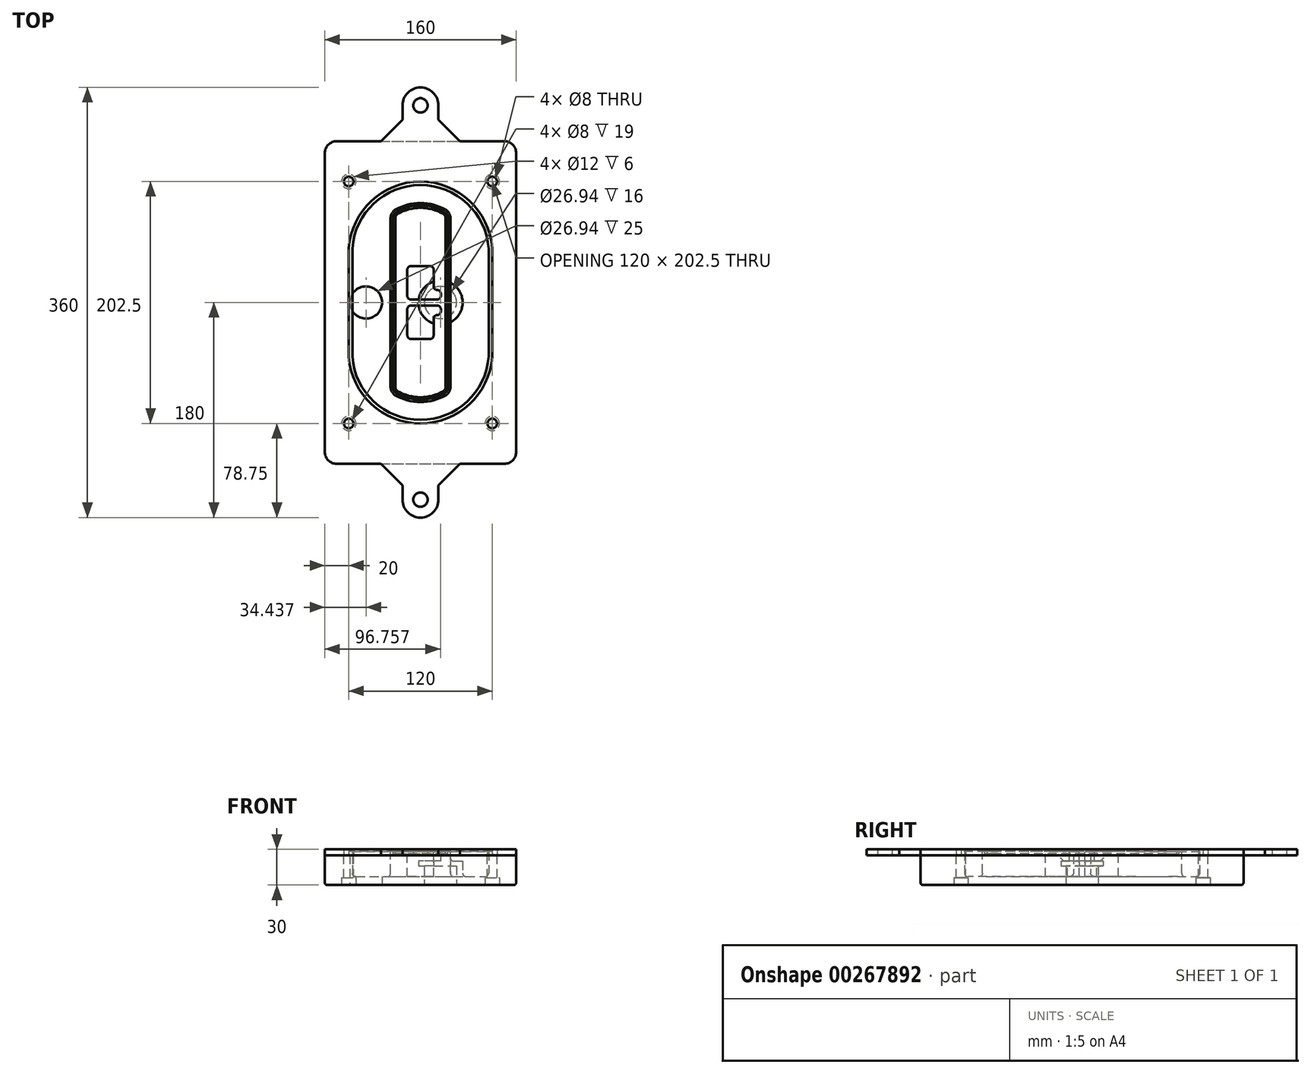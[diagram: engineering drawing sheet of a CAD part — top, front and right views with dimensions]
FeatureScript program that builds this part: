
annotation { "Feature Type Name" : "Feature", "Feature Type Description" : "" }
export const myFeature = defineFeature(function(context is Context, id is Id, definition is map)
    precondition{}
    {
        {
            var Q0;
            Q0=qCreatedBy(makeId("Top.planeOp"),FACE);
            var sketch = newSketch(context, id + "F0", { "sketchPlane" : qUnion([Q0])});
            skPoint(sketch, "E0.rect.middle", {"position": v(0, 0) * mm});
            skLineSegment(sketch, "E1.bottom", {"start": v(-70, -135) * mm, "end": v(70, -135) * mm});
            skLineSegment(sketch, "E1.top", {"start": v(-70, 135) * mm, "end": v(70, 135) * mm});
            skLineSegment(sketch, "E1.left", {"start": v(-80, -125) * mm, "end": v(-80, 125) * mm});
            skLineSegment(sketch, "E1.right", {"start": v(80, -125) * mm, "end": v(80, 125) * mm});
            skLineSegment(sketch, "E2", {"start": v(-80, 135) * mm, "end": v(80, -135) * mm, "construction": true});
            skLineSegment(sketch, "E3", {"start": v(80, 135) * mm, "end": v(-80, -135) * mm, "construction": true});
            skCircle(sketch, "E4", {"center": v(-60, 101.25) * mm, "radius": 4 * mm});
            skCircle(sketch, "E5", {"center": v(60, 101.25) * mm, "radius": 4 * mm});
            skCircle(sketch, "E6", {"center": v(60, -101.25) * mm, "radius": 4 * mm});
            skCircle(sketch, "E7", {"center": v(-60, -101.25) * mm, "radius": 4 * mm});
            skLineSegment(sketch, "E8", {"start": v(-60, 101.25) * mm, "end": v(60, 101.25) * mm, "construction": true});
            skLineSegment(sketch, "E9", {"start": v(60, 101.25) * mm, "end": v(60, -101.25) * mm, "construction": true});
            skLineSegment(sketch, "E10", {"start": v(60, -101.25) * mm, "end": v(-60, -101.25) * mm, "construction": true});
            skLineSegment(sketch, "E11", {"start": v(-60, -101.25) * mm, "end": v(-60, 101.25) * mm, "construction": true});
            skLineSegment(sketch, "E12", {"start": v(-60, 44.66) * mm, "end": v(-60, -44.66) * mm});
            skLineSegment(sketch, "E13", {"start": v(60, 44.66) * mm, "end": v(60, -44.66) * mm});
            skArc(sketch, "E14", {"start": v(59.98, 45.37) * mm, "mid": v(0, 101.25) * mm, "end": v(-59.98, 45.37) * mm});
            skArc(sketch, "E15", {"start": v(-59.98, -45.37) * mm, "mid": v(0, -101.25) * mm, "end": v(59.98, -45.37) * mm});
            skLineSegment(sketch, "E16", {"start": v(-60, 0) * mm, "end": v(60, 0) * mm, "construction": true});
            skPoint(sketch, "E17.visualSharp", {"position": v(-60, -45) * mm});
            skArc(sketch, "E17.filletArc", {"start": v(-60, -44.66) * mm, "mid": v(-60, -45.02) * mm, "end": v(-59.98, -45.37) * mm});
            skPoint(sketch, "E18.visualSharp", {"position": v(-60, 45) * mm});
            skArc(sketch, "E18.filletArc", {"start": v(-59.98, 45.37) * mm, "mid": v(-60, 45.02) * mm, "end": v(-60, 44.66) * mm});
            skPoint(sketch, "E19.visualSharp", {"position": v(60, 45) * mm});
            skArc(sketch, "E19.filletArc", {"start": v(60, 44.66) * mm, "mid": v(60, 45.02) * mm, "end": v(59.98, 45.37) * mm});
            skPoint(sketch, "E20.visualSharp", {"position": v(60, -45) * mm});
            skArc(sketch, "E20.filletArc", {"start": v(59.98, -45.37) * mm, "mid": v(60, -45.02) * mm, "end": v(60, -44.66) * mm});
            skPoint(sketch, "E21.visualSharp", {"position": v(-80, 135) * mm});
            skArc(sketch, "E21.filletArc", {"start": v(-70, 135) * mm, "mid": v(-77.07, 132.07) * mm, "end": v(-80, 125) * mm});
            skPoint(sketch, "E22.visualSharp", {"position": v(80, 135) * mm});
            skArc(sketch, "E22.filletArc", {"start": v(80, 125) * mm, "mid": v(77.07, 132.07) * mm, "end": v(70, 135) * mm});
            skPoint(sketch, "E23.visualSharp", {"position": v(80, -135) * mm});
            skArc(sketch, "E23.filletArc", {"start": v(70, -135) * mm, "mid": v(77.07, -132.07) * mm, "end": v(80, -125) * mm});
            skPoint(sketch, "E24.visualSharp", {"position": v(-80, -135) * mm});
            skArc(sketch, "E24.filletArc", {"start": v(-80, -125) * mm, "mid": v(-77.07, -132.07) * mm, "end": v(-70, -135) * mm});
            skArc(sketch, "E25.0", {"start": v(57, 44.66) * mm, "mid": v(57, 44.9) * mm, "end": v(56.98, 45.16) * mm});
            skLineSegment(sketch, "E25.1", {"start": v(57, 44.66) * mm, "end": v(57, -44.66) * mm});
            skArc(sketch, "E25.2", {"start": v(56.98, -45.16) * mm, "mid": v(57, -44.9) * mm, "end": v(57, -44.66) * mm});
            skArc(sketch, "E25.3", {"start": v(-56.98, -45.16) * mm, "mid": v(0, -98.25) * mm, "end": v(56.98, -45.16) * mm});
            skArc(sketch, "E25.4", {"start": v(-57, -44.66) * mm, "mid": v(-57, -44.9) * mm, "end": v(-56.98, -45.16) * mm});
            skArc(sketch, "E25.5", {"start": v(56.98, 45.16) * mm, "mid": v(0, 98.25) * mm, "end": v(-56.98, 45.16) * mm});
            skLineSegment(sketch, "E25.6", {"start": v(-57, 44.66) * mm, "end": v(-57, -44.66) * mm});
            skArc(sketch, "E25.7", {"start": v(-56.98, 45.16) * mm, "mid": v(-57, 44.9) * mm, "end": v(-57, 44.66) * mm});
            skArc(sketch, "E26.0", {"start": v(-63.97, 45.65) * mm, "mid": v(-64, 45.16) * mm, "end": v(-64, 44.66) * mm});
            skArc(sketch, "E26.1", {"start": v(63.97, 45.65) * mm, "mid": v(0, 105.25) * mm, "end": v(-63.97, 45.65) * mm});
            skArc(sketch, "E26.2", {"start": v(64, 44.66) * mm, "mid": v(64, 45.16) * mm, "end": v(63.97, 45.65) * mm});
            skLineSegment(sketch, "E26.3", {"start": v(64, 44.66) * mm, "end": v(64, -44.66) * mm});
            skArc(sketch, "E26.4", {"start": v(63.97, -45.65) * mm, "mid": v(64, -45.16) * mm, "end": v(64, -44.66) * mm});
            skLineSegment(sketch, "E26.5", {"start": v(-64, 44.66) * mm, "end": v(-64, -44.66) * mm});
            skArc(sketch, "E26.6", {"start": v(-63.97, -45.65) * mm, "mid": v(0, -105.25) * mm, "end": v(63.97, -45.65) * mm});
            skArc(sketch, "E26.7", {"start": v(-64, -44.66) * mm, "mid": v(-64, -45.16) * mm, "end": v(-63.97, -45.65) * mm});
            skSolve(sketch);
        }
        {
            var Q0;
            Q0=makeQuery(id+"F0.imprint","IMPRINT",FACE,{"disambiguationData":[TD([[makeQuery(id+"F0.imprint","IMPRINT",EDGE,{"derivedFrom":sQuery(id+"F0.wireOp",EDGE,"E1.bottom")}),1.0]])]});
            var Q1;
            Q1=makeQuery(id+"F0.imprint","IMPRINT",FACE,{"disambiguationData":[TD([[makeQuery(id+"F0.imprint","IMPRINT",EDGE,{"derivedFrom":sQuery(id+"F0.wireOp",EDGE,"E12")}),1.0]])]});
            var Q2;
            Q2=makeQuery(id+"F0.imprint","IMPRINT",FACE,{"disambiguationData":[TD([[makeQuery(id+"F0.imprint","IMPRINT",EDGE,{"derivedFrom":sQuery(id+"F0.wireOp",EDGE,"E25.0")}),1.0]])]});
            var Q3;
            Q3=makeQuery(id+"F0.imprint","IMPRINT",FACE,{"disambiguationData":[TD([[makeQuery(id+"F0.imprint","IMPRINT",EDGE,{"derivedFrom":sQuery(id+"F0.wireOp",EDGE,"E12")}),-1.0]])]});
            extrude(context, id + "F1", {"entities" : qUnion([Q0, Q1, Q2, Q3]), "oppositeDirection" : true, "depth" : 25 * mm});
        }
        {
            var Q0;
            Q0=makeQuery(id+"F0.imprint","IMPRINT",FACE,{"disambiguationData":[TD([[makeQuery(id+"F0.imprint","IMPRINT",EDGE,{"derivedFrom":sQuery(id+"F0.wireOp",EDGE,"E12")}),1.0]])]});
            extrude(context, id + "F2", {"entities" : qUnion([Q0]), "operationType" : NewBodyOperationType.ADD, "depth" : 3 * mm});
        }
        {
            var Q0;
            Q0=makeQuery(id+"F0.imprint","IMPRINT",FACE,{"disambiguationData":[TD([[makeQuery(id+"F0.imprint","IMPRINT",EDGE,{"derivedFrom":sQuery(id+"F0.wireOp",EDGE,"E25.0")}),1.0]])]});
            extrude(context, id + "F3", {"entities" : qUnion([Q0]), "operationType" : NewBodyOperationType.REMOVE, "oppositeDirection" : true, "depth" : 18 * mm});
        }
        {
            var Q0;
            Q0=makeQuery(id+"F2.opExtrude","CAP_FACE",FACE,{"disambiguationData":[OSD([sQuery(id+"F0.wireOp",EDGE,"E12"),sQuery(id+"F0.wireOp",EDGE,"E13"),sQuery(id+"F0.wireOp",EDGE,"E14"),sQuery(id+"F0.wireOp",EDGE,"E15"),sQuery(id+"F0.wireOp",EDGE,"E17.filletArc"),sQuery(id+"F0.wireOp",EDGE,"E18.filletArc"),sQuery(id+"F0.wireOp",EDGE,"E19.filletArc"),sQuery(id+"F0.wireOp",EDGE,"E20.filletArc"),sQuery(id+"F0.wireOp",EDGE,"E25.0"),sQuery(id+"F0.wireOp",EDGE,"E25.1"),sQuery(id+"F0.wireOp",EDGE,"E25.2"),sQuery(id+"F0.wireOp",EDGE,"E25.3"),sQuery(id+"F0.wireOp",EDGE,"E25.4"),sQuery(id+"F0.wireOp",EDGE,"E25.5"),sQuery(id+"F0.wireOp",EDGE,"E25.6"),sQuery(id+"F0.wireOp",EDGE,"E25.7")])],"isStart":false});
            var sketch = newSketch(context, id + "F4", { "sketchPlane" : qUnion([Q0])});
            skArc(sketch, "E27.0", {"start": v(-20.99, -77.65) * mm, "mid": v(0, -83.25) * mm, "end": v(20.99, -77.65) * mm});
            skArc(sketch, "E28.0", {"start": v(20.99, 77.65) * mm, "mid": v(0, 83.25) * mm, "end": v(-20.99, 77.65) * mm});
            skLineSegment(sketch, "E29", {"start": v(-25, 70.71) * mm, "end": v(-25, -70.71) * mm});
            skLineSegment(sketch, "E30", {"start": v(25, 70.71) * mm, "end": v(25, -70.71) * mm});
            skLineSegment(sketch, "E31", {"start": v(-25, 75.03) * mm, "end": v(25, 75.03) * mm, "construction": true});
            skLineSegment(sketch, "E32", {"start": v(-25, -75.03) * mm, "end": v(25, -75.03) * mm, "construction": true});
            skPoint(sketch, "E33.visualSharp", {"position": v(-25, 75.03) * mm});
            skArc(sketch, "E33.filletArc", {"start": v(-20.99, 77.65) * mm, "mid": v(-23.92, 74.72) * mm, "end": v(-25, 70.71) * mm});
            skPoint(sketch, "E34.visualSharp", {"position": v(25, 75.03) * mm});
            skArc(sketch, "E34.filletArc", {"start": v(25, 70.71) * mm, "mid": v(23.92, 74.72) * mm, "end": v(20.99, 77.65) * mm});
            skPoint(sketch, "E35.visualSharp", {"position": v(25, -75.03) * mm});
            skArc(sketch, "E35.filletArc", {"start": v(20.99, -77.65) * mm, "mid": v(23.92, -74.72) * mm, "end": v(25, -70.71) * mm});
            skPoint(sketch, "E36.visualSharp", {"position": v(-25, -75.03) * mm});
            skArc(sketch, "E36.filletArc", {"start": v(-25, -70.71) * mm, "mid": v(-23.92, -74.72) * mm, "end": v(-20.99, -77.65) * mm});
            skArc(sketch, "E37.0", {"start": v(56.98, 45.16) * mm, "mid": v(0, 98.25) * mm, "end": v(-56.98, 45.16) * mm});
            skArc(sketch, "E37.1", {"start": v(-56.98, 45.16) * mm, "mid": v(-57, 44.9) * mm, "end": v(-57, 44.66) * mm});
            skLineSegment(sketch, "E37.2", {"start": v(-57, 44.66) * mm, "end": v(-57, -44.66) * mm});
            skArc(sketch, "E37.3", {"start": v(-57, -44.66) * mm, "mid": v(-57, -44.9) * mm, "end": v(-56.98, -45.16) * mm});
            skArc(sketch, "E37.4", {"start": v(-56.98, -45.16) * mm, "mid": v(0, -98.25) * mm, "end": v(56.98, -45.16) * mm});
            skArc(sketch, "E37.5", {"start": v(56.98, -45.16) * mm, "mid": v(57, -44.9) * mm, "end": v(57, -44.66) * mm});
            skLineSegment(sketch, "E37.6", {"start": v(57, 44.66) * mm, "end": v(57, -44.66) * mm});
            skArc(sketch, "E37.7", {"start": v(57, 44.66) * mm, "mid": v(57, 44.9) * mm, "end": v(56.98, 45.16) * mm});
            skLineSegment(sketch, "E38.0", {"start": v(23, 70.71) * mm, "end": v(23, -70.71) * mm});
            skArc(sketch, "E38.1", {"start": v(19.99, -75.92) * mm, "mid": v(22.2, -73.72) * mm, "end": v(23, -70.71) * mm});
            skArc(sketch, "E38.2", {"start": v(-19.99, -75.92) * mm, "mid": v(0, -81.25) * mm, "end": v(19.99, -75.92) * mm});
            skArc(sketch, "E38.3", {"start": v(-23, -70.71) * mm, "mid": v(-22.2, -73.72) * mm, "end": v(-19.99, -75.92) * mm});
            skLineSegment(sketch, "E38.4", {"start": v(-23, 70.71) * mm, "end": v(-23, -70.71) * mm});
            skArc(sketch, "E38.5", {"start": v(23, 70.71) * mm, "mid": v(22.2, 73.72) * mm, "end": v(19.99, 75.92) * mm});
            skArc(sketch, "E38.6", {"start": v(-19.99, 75.92) * mm, "mid": v(-22.2, 73.72) * mm, "end": v(-23, 70.71) * mm});
            skArc(sketch, "E38.7", {"start": v(19.99, 75.92) * mm, "mid": v(0, 81.25) * mm, "end": v(-19.99, 75.92) * mm});
            skArc(sketch, "E39.0", {"start": v(21, 70.71) * mm, "mid": v(20.46, 72.72) * mm, "end": v(19, 74.18) * mm});
            skLineSegment(sketch, "E39.1", {"start": v(21, 70.71) * mm, "end": v(21, -70.71) * mm});
            skArc(sketch, "E39.2", {"start": v(19, -74.18) * mm, "mid": v(20.46, -72.72) * mm, "end": v(21, -70.71) * mm});
            skArc(sketch, "E39.3", {"start": v(-19, -74.18) * mm, "mid": v(0, -79.25) * mm, "end": v(19, -74.18) * mm});
            skArc(sketch, "E39.4", {"start": v(-21, -70.71) * mm, "mid": v(-20.46, -72.72) * mm, "end": v(-19, -74.18) * mm});
            skArc(sketch, "E39.5", {"start": v(19, 74.18) * mm, "mid": v(0, 79.25) * mm, "end": v(-19, 74.18) * mm});
            skLineSegment(sketch, "E39.6", {"start": v(-21, 70.71) * mm, "end": v(-21, -70.71) * mm});
            skArc(sketch, "E39.7", {"start": v(-19, 74.18) * mm, "mid": v(-20.46, 72.72) * mm, "end": v(-21, 70.71) * mm});
            skLineSegment(sketch, "E40", {"start": v(-25, 0) * mm, "end": v(25, 0) * mm, "construction": true});
            skLineSegment(sketch, "E41", {"start": v(-11, 5.5) * mm, "end": v(-11, 27.5) * mm});
            skLineSegment(sketch, "E42", {"start": v(-8, 30.5) * mm, "end": v(8, 30.5) * mm});
            skLineSegment(sketch, "E43", {"start": v(11, 27.5) * mm, "end": v(11, 13.5) * mm});
            skLineSegment(sketch, "E44", {"start": v(14, 10.5) * mm, "end": v(14, 10.5) * mm});
            skLineSegment(sketch, "E45", {"start": v(17, 7.5) * mm, "end": v(17, 5.5) * mm});
            skLineSegment(sketch, "E46", {"start": v(14, 2.5) * mm, "end": v(-8, 2.5) * mm});
            skPoint(sketch, "E47.visualSharp", {"position": v(-11, 30.5) * mm});
            skArc(sketch, "E47.filletArc", {"start": v(-8, 30.5) * mm, "mid": v(-10.12, 29.62) * mm, "end": v(-11, 27.5) * mm});
            skPoint(sketch, "E48.visualSharp", {"position": v(11, 30.5) * mm});
            skArc(sketch, "E48.filletArc", {"start": v(11, 27.5) * mm, "mid": v(10.12, 29.62) * mm, "end": v(8, 30.5) * mm});
            skPoint(sketch, "E49.visualSharp", {"position": v(11, 10.5) * mm});
            skArc(sketch, "E49.filletArc", {"start": v(11, 13.5) * mm, "mid": v(11.88, 11.38) * mm, "end": v(14, 10.5) * mm});
            skPoint(sketch, "E50.visualSharp", {"position": v(17, 10.5) * mm});
            skArc(sketch, "E50.filletArc", {"start": v(17, 7.5) * mm, "mid": v(16.12, 9.62) * mm, "end": v(14, 10.5) * mm});
            skPoint(sketch, "E51.visualSharp", {"position": v(17, 2.5) * mm});
            skArc(sketch, "E51.filletArc", {"start": v(14, 2.5) * mm, "mid": v(16.12, 3.38) * mm, "end": v(17, 5.5) * mm});
            skPoint(sketch, "E52.visualSharp", {"position": v(-11, 2.5) * mm});
            skArc(sketch, "E52.filletArc", {"start": v(-11, 5.5) * mm, "mid": v(-10.12, 3.38) * mm, "end": v(-8, 2.5) * mm});
            skLineSegment(sketch, "E53.0.MirrorCS", {"start": v(14, -2.5) * mm, "end": v(-8, -2.5) * mm});
            skArc(sketch, "E54.0.MirrorCS", {"start": v(-11, -5.5) * mm, "mid": v(-10.12, -3.38) * mm, "end": v(-8, -2.5) * mm});
            skLineSegment(sketch, "E55.0.MirrorCS", {"start": v(-11, -5.5) * mm, "end": v(-11, -27.5) * mm});
            skArc(sketch, "E56.0.MirrorCS", {"start": v(-8, -30.5) * mm, "mid": v(-10.12, -29.62) * mm, "end": v(-11, -27.5) * mm});
            skLineSegment(sketch, "E57.0.MirrorCS", {"start": v(-8, -30.5) * mm, "end": v(8, -30.5) * mm});
            skArc(sketch, "E58.0.MirrorCS", {"start": v(11, -27.5) * mm, "mid": v(10.12, -29.62) * mm, "end": v(8, -30.5) * mm});
            skLineSegment(sketch, "E59.0.MirrorCS", {"start": v(11, -27.5) * mm, "end": v(11, -13.5) * mm});
            skArc(sketch, "E60.0.MirrorCS", {"start": v(11, -13.5) * mm, "mid": v(11.88, -11.38) * mm, "end": v(14, -10.5) * mm});
            skArc(sketch, "E61.0.MirrorCS", {"start": v(17, -7.5) * mm, "mid": v(16.12, -9.62) * mm, "end": v(14, -10.5) * mm});
            skLineSegment(sketch, "E62.0.MirrorCS", {"start": v(17, -7.5) * mm, "end": v(17, -5.5) * mm});
            skArc(sketch, "E63.0.MirrorCS", {"start": v(14, -2.5) * mm, "mid": v(16.12, -3.38) * mm, "end": v(17, -5.5) * mm});
            skSolve(sketch);
        }
        {
            var Q0;
            Q0=makeQuery(id+"F4.imprint","IMPRINT",FACE,{"disambiguationData":[TD([[makeQuery(id+"F4.imprint","IMPRINT",EDGE,{"derivedFrom":sQuery(id+"F4.wireOp",EDGE,"E27.0")}),1.0]])]});
            var Q1;
            Q1=makeQuery(id+"F4.imprint","IMPRINT",FACE,{"disambiguationData":[TD([[makeQuery(id+"F4.imprint","IMPRINT",EDGE,{"derivedFrom":sQuery(id+"F4.wireOp",EDGE,"E38.0")}),-1.0]])]});
            var Q2;
            Q2=makeQuery(id+"F4.imprint","IMPRINT",FACE,{"disambiguationData":[TD([[makeQuery(id+"F4.imprint","IMPRINT",EDGE,{"derivedFrom":sQuery(id+"F4.wireOp",EDGE,"E39.0")}),1.0]])]});
            extrude(context, id + "F5", {"entities" : qUnion([Q0, Q1, Q2]), "operationType" : NewBodyOperationType.ADD, "endBound" : BoundingType.UP_TO_NEXT, "oppositeDirection" : true, "depth" : 25 * mm});
        }
        {
            var Q0;
            Q0=makeQuery(id+"F4.imprint","IMPRINT",FACE,{"disambiguationData":[TD([[makeQuery(id+"F4.imprint","IMPRINT",EDGE,{"derivedFrom":sQuery(id+"F4.wireOp",EDGE,"E38.0")}),-1.0]])]});
            extrude(context, id + "F6", {"entities" : qUnion([Q0]), "operationType" : NewBodyOperationType.REMOVE, "oppositeDirection" : true, "depth" : 2 * mm});
        }
        {
            var Q0;
            Q0=makeQuery(id+"F1.opExtrude","CAP_FACE",FACE,{"disambiguationData":[OSD([sQuery(id+"F0.wireOp",EDGE,"E1.bottom"),sQuery(id+"F0.wireOp",EDGE,"E1.top"),sQuery(id+"F0.wireOp",EDGE,"E1.left"),sQuery(id+"F0.wireOp",EDGE,"E1.right"),sQuery(id+"F0.wireOp",EDGE,"E4"),sQuery(id+"F0.wireOp",EDGE,"E5"),sQuery(id+"F0.wireOp",EDGE,"E6"),sQuery(id+"F0.wireOp",EDGE,"E7"),sQuery(id+"F0.wireOp",EDGE,"E21.filletArc"),sQuery(id+"F0.wireOp",EDGE,"E22.filletArc"),sQuery(id+"F0.wireOp",EDGE,"E23.filletArc"),sQuery(id+"F0.wireOp",EDGE,"E24.filletArc")])],"isStart":false});
            var sketch = newSketch(context, id + "F7", { "sketchPlane" : qUnion([Q0])});
            skCircle(sketch, "E64", {"center": v(16.76, 0) * mm, "radius": 13.47 * mm});
            skCircle(sketch, "E65", {"center": v(-45.56, 0) * mm, "radius": 13.47 * mm});
            skLineSegment(sketch, "E66", {"start": v(80, 0) * mm, "end": v(-80, 0) * mm});
            skCircle(sketch, "E67", {"center": v(16.76, 0) * mm, "radius": 18.47 * mm});
            skCircle(sketch, "E68", {"center": v(60, -101.25) * mm, "radius": 6 * mm});
            skCircle(sketch, "E69", {"center": v(-60, -101.25) * mm, "radius": 6 * mm});
            skCircle(sketch, "E70", {"center": v(-60, 101.25) * mm, "radius": 6 * mm});
            skCircle(sketch, "E71", {"center": v(60, 101.25) * mm, "radius": 6 * mm});
            skSolve(sketch);
        }
        {
            var Q0;
            {var subQ1=sQuery(id+"F7.wireOp",EDGE,"E66");var subQ4=sQuery(id+"F7.wireOp",EDGE,"E64");var subQ6=makeQuery(id+"F7.imprint","INTERSECT",VERTEX,{"disambiguationData":[OD(0.0)],"derivedFrom":[subQ4,subQ1]});Q0=makeQuery(id+"F7.imprint","IMPRINT",FACE,{"disambiguationData":[TD([[makeQuery(id+"F7.imprint","IMPRINT",EDGE,{"disambiguationData":[TD([[subQ6,-1.0]])],"derivedFrom":subQ4}),-1.0]])]});}
            var Q1;
            {var subQ0=sQuery(id+"F7.wireOp",EDGE,"E66");var subQ1=sQuery(id+"F7.wireOp",EDGE,"E64");var subQ3=makeQuery(id+"F7.imprint","INTERSECT",VERTEX,{"disambiguationData":[OD(0.0)],"derivedFrom":[subQ1,subQ0]});Q1=makeQuery(id+"F7.imprint","IMPRINT",FACE,{"disambiguationData":[TD([[makeQuery(id+"F7.imprint","IMPRINT",EDGE,{"disambiguationData":[TD([[subQ3,-1.0]])],"derivedFrom":subQ1}),1.0]])]});}
            var Q2;
            {var subQ0=sQuery(id+"F7.wireOp",EDGE,"E66");var subQ1=sQuery(id+"F7.wireOp",EDGE,"E64");var subQ3=makeQuery(id+"F7.imprint","INTERSECT",VERTEX,{"disambiguationData":[OD(0.0)],"derivedFrom":[subQ1,subQ0]});Q2=makeQuery(id+"F7.imprint","IMPRINT",FACE,{"disambiguationData":[TD([[makeQuery(id+"F7.imprint","IMPRINT",EDGE,{"disambiguationData":[TD([[subQ3,1.0]])],"derivedFrom":subQ1}),1.0]])]});}
            var Q3;
            {var subQ1=sQuery(id+"F7.wireOp",EDGE,"E66");var subQ4=sQuery(id+"F7.wireOp",EDGE,"E64");var subQ6=makeQuery(id+"F7.imprint","INTERSECT",VERTEX,{"disambiguationData":[OD(0.0)],"derivedFrom":[subQ4,subQ1]});Q3=makeQuery(id+"F7.imprint","IMPRINT",FACE,{"disambiguationData":[TD([[makeQuery(id+"F7.imprint","IMPRINT",EDGE,{"disambiguationData":[TD([[subQ6,1.0]])],"derivedFrom":subQ4}),-1.0]])]});}
            extrude(context, id + "F8", {"entities" : qUnion([Q0, Q1, Q2, Q3]), "operationType" : NewBodyOperationType.ADD, "oppositeDirection" : true, "depth" : 20 * mm});
        }
        {
            var Q0;
            {var subQ0=sQuery(id+"F7.wireOp",EDGE,"E66");var subQ1=sQuery(id+"F7.wireOp",EDGE,"E64");var subQ3=makeQuery(id+"F7.imprint","INTERSECT",VERTEX,{"disambiguationData":[OD(0.0)],"derivedFrom":[subQ1,subQ0]});Q0=makeQuery(id+"F7.imprint","IMPRINT",FACE,{"disambiguationData":[TD([[makeQuery(id+"F7.imprint","IMPRINT",EDGE,{"disambiguationData":[TD([[subQ3,-1.0]])],"derivedFrom":subQ1}),1.0]])]});}
            var Q1;
            {var subQ0=sQuery(id+"F7.wireOp",EDGE,"E66");var subQ1=sQuery(id+"F7.wireOp",EDGE,"E64");var subQ3=makeQuery(id+"F7.imprint","INTERSECT",VERTEX,{"disambiguationData":[OD(0.0)],"derivedFrom":[subQ1,subQ0]});Q1=makeQuery(id+"F7.imprint","IMPRINT",FACE,{"disambiguationData":[TD([[makeQuery(id+"F7.imprint","IMPRINT",EDGE,{"disambiguationData":[TD([[subQ3,1.0]])],"derivedFrom":subQ1}),1.0]])]});}
            extrude(context, id + "F9", {"entities" : qUnion([Q0, Q1]), "operationType" : NewBodyOperationType.REMOVE, "oppositeDirection" : true, "depth" : 16 * mm});
        }
        {
            var Q0;
            {var subQ0=sQuery(id+"F7.wireOp",EDGE,"E66");var subQ1=sQuery(id+"F7.wireOp",EDGE,"E65");var subQ3=makeQuery(id+"F7.imprint","INTERSECT",VERTEX,{"disambiguationData":[OD(0.0)],"derivedFrom":[subQ1,subQ0]});Q0=makeQuery(id+"F7.imprint","IMPRINT",FACE,{"disambiguationData":[TD([[makeQuery(id+"F7.imprint","IMPRINT",EDGE,{"disambiguationData":[TD([[subQ3,-1.0]])],"derivedFrom":subQ1}),1.0]])]});}
            var Q1;
            {var subQ0=sQuery(id+"F7.wireOp",EDGE,"E66");var subQ1=sQuery(id+"F7.wireOp",EDGE,"E65");var subQ3=makeQuery(id+"F7.imprint","INTERSECT",VERTEX,{"disambiguationData":[OD(0.0)],"derivedFrom":[subQ1,subQ0]});Q1=makeQuery(id+"F7.imprint","IMPRINT",FACE,{"disambiguationData":[TD([[makeQuery(id+"F7.imprint","IMPRINT",EDGE,{"disambiguationData":[TD([[subQ3,1.0]])],"derivedFrom":subQ1}),1.0]])]});}
            extrude(context, id + "F10", {"entities" : qUnion([Q0, Q1]), "operationType" : NewBodyOperationType.REMOVE, "oppositeDirection" : true, "depth" : 25 * mm});
        }
        {
            var Q0;
            Q0=makeQuery(id+"F7.imprint","IMPRINT",FACE,{"disambiguationData":[TD([[makeQuery(id+"F7.imprint","IMPRINT",EDGE,{"derivedFrom":sQuery(id+"F7.wireOp",EDGE,"E68")}),1.0]])]});
            var Q1;
            Q1=makeQuery(id+"F7.imprint","IMPRINT",FACE,{"disambiguationData":[TD([[makeQuery(id+"F7.imprint","IMPRINT",EDGE,{"derivedFrom":makeQuery(id+"F1.opExtrude","CAP_EDGE",EDGE,{"disambiguationData":[OSD([sQuery(id+"F0.wireOp",EDGE,"E5")])],"isStart":false})}),-1.0]])]});
            var Q2;
            Q2=makeQuery(id+"F7.imprint","IMPRINT",FACE,{"disambiguationData":[TD([[makeQuery(id+"F7.imprint","IMPRINT",EDGE,{"derivedFrom":sQuery(id+"F7.wireOp",EDGE,"E69")}),1.0]])]});
            var Q3;
            Q3=makeQuery(id+"F7.imprint","IMPRINT",FACE,{"disambiguationData":[TD([[makeQuery(id+"F7.imprint","IMPRINT",EDGE,{"derivedFrom":makeQuery(id+"F1.opExtrude","CAP_EDGE",EDGE,{"disambiguationData":[OSD([sQuery(id+"F0.wireOp",EDGE,"E4")])],"isStart":false})}),-1.0]])]});
            var Q4;
            Q4=makeQuery(id+"F7.imprint","IMPRINT",FACE,{"disambiguationData":[TD([[makeQuery(id+"F7.imprint","IMPRINT",EDGE,{"derivedFrom":sQuery(id+"F7.wireOp",EDGE,"E70")}),1.0]])]});
            var Q5;
            Q5=makeQuery(id+"F7.imprint","IMPRINT",FACE,{"disambiguationData":[TD([[makeQuery(id+"F7.imprint","IMPRINT",EDGE,{"derivedFrom":makeQuery(id+"F1.opExtrude","CAP_EDGE",EDGE,{"disambiguationData":[OSD([sQuery(id+"F0.wireOp",EDGE,"E7")])],"isStart":false})}),-1.0]])]});
            var Q6;
            Q6=makeQuery(id+"F7.imprint","IMPRINT",FACE,{"disambiguationData":[TD([[makeQuery(id+"F7.imprint","IMPRINT",EDGE,{"derivedFrom":sQuery(id+"F7.wireOp",EDGE,"E71")}),1.0]])]});
            var Q7;
            Q7=makeQuery(id+"F7.imprint","IMPRINT",FACE,{"disambiguationData":[TD([[makeQuery(id+"F7.imprint","IMPRINT",EDGE,{"derivedFrom":makeQuery(id+"F1.opExtrude","CAP_EDGE",EDGE,{"disambiguationData":[OSD([sQuery(id+"F0.wireOp",EDGE,"E6")])],"isStart":false})}),-1.0]])]});
            extrude(context, id + "F11", {"entities" : qUnion([Q0, Q1, Q2, Q3, Q4, Q5, Q6, Q7]), "operationType" : NewBodyOperationType.REMOVE, "oppositeDirection" : true, "depth" : 6 * mm});
        }
        {
            var Q0;
            Q0=makeQuery(id+"F9.boolean.opBoolean","COPY",FACE,{"derivedFrom":makeQuery(id+"F9.opExtrude","CAP_FACE",FACE,{"disambiguationData":[OSD([sQuery(id+"F7.wireOp",EDGE,"E64")])],"isStart":false})});
            var sketch = newSketch(context, id + "F12", { "sketchPlane" : qUnion([Q0])});
            skArc(sketch, "E72.0", {"start": v(11, 17.55) * mm, "mid": v(2.57, 11.82) * mm, "end": v(-1.54, 2.5) * mm});
            skArc(sketch, "E72.1", {"start": v(-1.54, -2.5) * mm, "mid": v(2.57, -11.82) * mm, "end": v(11, -17.55) * mm});
            skLineSegment(sketch, "E73", {"start": v(-1.54, -2.5) * mm, "end": v(14, -2.5) * mm});
            skLineSegment(sketch, "E74.0", {"start": v(14, 2.5) * mm, "end": v(-1.54, 2.5) * mm});
            skArc(sketch, "E74.1", {"start": v(14, 2.5) * mm, "mid": v(16.12, 3.38) * mm, "end": v(17, 5.5) * mm});
            skLineSegment(sketch, "E74.2", {"start": v(17, 7.5) * mm, "end": v(17, 5.5) * mm});
            skArc(sketch, "E74.3", {"start": v(17, 7.5) * mm, "mid": v(16.12, 9.62) * mm, "end": v(14, 10.5) * mm});
            skArc(sketch, "E74.4", {"start": v(11, 13.5) * mm, "mid": v(11.88, 11.38) * mm, "end": v(14, 10.5) * mm});
            skLineSegment(sketch, "E74.5", {"start": v(11, 17.55) * mm, "end": v(11, 13.5) * mm});
            skLineSegment(sketch, "E74.7", {"start": v(14, -2.5) * mm, "end": v(-1.54, -2.5) * mm});
            skArc(sketch, "E74.8", {"start": v(14, -2.5) * mm, "mid": v(16.12, -3.38) * mm, "end": v(17, -5.5) * mm});
            skLineSegment(sketch, "E74.9", {"start": v(17, -7.5) * mm, "end": v(17, -5.5) * mm});
            skArc(sketch, "E74.10", {"start": v(17, -7.5) * mm, "mid": v(16.12, -9.62) * mm, "end": v(14, -10.5) * mm});
            skArc(sketch, "E74.11", {"start": v(11, -13.5) * mm, "mid": v(11.88, -11.38) * mm, "end": v(14, -10.5) * mm});
            skLineSegment(sketch, "E74.12", {"start": v(11, -17.55) * mm, "end": v(11, -13.5) * mm});
            skPoint(sketch, "E75.orphan", {"position": v(11, -27.5) * mm});
            skPoint(sketch, "E76.orphan", {"position": v(-8, -2.5) * mm});
            skPoint(sketch, "E77.orphan", {"position": v(-8, 2.5) * mm});
            skPoint(sketch, "E78.orphan", {"position": v(11, 27.5) * mm});
            skSolve(sketch);
        }
        {
            var Q0;
            {var subQ7=sQuery(id+"F12.wireOp",EDGE,"E72.0");var subQ14=sQuery(id+"F12.wireOp",EDGE,"E72.1");var subQ16=sQuery(id+"F12.wireOp",EDGE,"E74.1");var subQ18=sQuery(id+"F12.wireOp",EDGE,"E74.8");Q0=qUnion([makeQuery(id+"F12.imprint","IMPRINT",FACE,{"disambiguationData":[TD([[makeQuery(id+"F12.imprint","IMPRINT",EDGE,{"derivedFrom":subQ7}),1.0]])]}),makeQuery(id+"F12.imprint","IMPRINT",FACE,{"disambiguationData":[TD([[makeQuery(id+"F12.imprint","IMPRINT",EDGE,{"derivedFrom":subQ14}),1.0]])]}),makeQuery(id+"F12.imprint","IMPRINT",FACE,{"disambiguationData":[TD([[makeQuery(id+"F12.imprint","IMPRINT",EDGE,{"derivedFrom":subQ16}),1.0]])]}),makeQuery(id+"F12.imprint","IMPRINT",FACE,{"disambiguationData":[TD([[makeQuery(id+"F12.imprint","IMPRINT",EDGE,{"derivedFrom":subQ18}),-1.0]])]})]);}
            var Q1;
            Q1=makeQuery(id+"F5.boolean.opBoolean","SPLIT",FACE,{"disambiguationData":[TD([makeQuery(id+"F5.opExtrude","SWEPT_FACE",FACE,{"disambiguationData":[OSD([sQuery(id+"F4.wireOp",EDGE,"E41")])]})])],"derivedFrom":makeQuery(id+"F3.boolean.opBoolean","COPY",FACE,{"derivedFrom":makeQuery(id+"F3.opExtrude","CAP_FACE",FACE,{"disambiguationData":[OSD([sQuery(id+"F0.wireOp",EDGE,"E25.0"),sQuery(id+"F0.wireOp",EDGE,"E25.1"),sQuery(id+"F0.wireOp",EDGE,"E25.2"),sQuery(id+"F0.wireOp",EDGE,"E25.3"),sQuery(id+"F0.wireOp",EDGE,"E25.4"),sQuery(id+"F0.wireOp",EDGE,"E25.5"),sQuery(id+"F0.wireOp",EDGE,"E25.6"),sQuery(id+"F0.wireOp",EDGE,"E25.7")])],"isStart":false})})});
            extrude(context, id + "F13", {"entities" : qUnion([Q0]), "operationType" : NewBodyOperationType.REMOVE, "endBound" : BoundingType.UP_TO_SURFACE, "endBoundEntityFace" : qUnion([Q1]), "depth" : 25 * mm});
        }
        {
            var Q0;
            Q0=makeQuery(id+"F3.boolean.opBoolean","COPY",EDGE,{"derivedFrom":makeQuery(id+"F3.opExtrude","CAP_EDGE",EDGE,{"disambiguationData":[OSD([sQuery(id+"F0.wireOp",EDGE,"E25.6")])],"isStart":false})});
            var Q1;
            Q1=makeQuery(id+"F8.boolean.opBoolean","INTERSECT",EDGE,{"derivedFrom":[makeQuery(id+"F5.opExtrude","SWEPT_FACE",FACE,{"disambiguationData":[OSD([sQuery(id+"F4.wireOp",EDGE,"E30")])]}),makeQuery(id+"F8.opExtrude","CAP_FACE",FACE,{"disambiguationData":[OSD([sQuery(id+"F7.wireOp",EDGE,"E67")])],"isStart":false})]});
            var Q2;
            Q2=makeQuery(id+"F8.boolean.opBoolean","INTERSECT",EDGE,{"disambiguationData":[OD(1.0)],"derivedFrom":[makeQuery(id+"F5.opExtrude","SWEPT_FACE",FACE,{"disambiguationData":[OSD([sQuery(id+"F4.wireOp",EDGE,"E30")])]}),makeQuery(id+"F8.opExtrude","SWEPT_FACE",FACE,{"disambiguationData":[OSD([sQuery(id+"F7.wireOp",EDGE,"E67")])]})]});
            var Q3;
            {var subQ0=sQuery(id+"F4.wireOp",EDGE,"E30");Q3=makeQuery(id+"F8.boolean.opBoolean","SPLIT",EDGE,{"disambiguationData":[TD([makeQuery(id+"F5.opExtrude","SWEPT_FACE",FACE,{"disambiguationData":[OSD([sQuery(id+"F4.wireOp",EDGE,"E35.filletArc")])]})])],"derivedFrom":makeQuery(id+"F5.opExtrude","CAP_EDGE",EDGE,{"disambiguationData":[OSD([subQ0])],"isStart":false})});}
            var Q4;
            {var subQ0=sQuery(id+"F0.wireOp",EDGE,"E25.7");var subQ1=sQuery(id+"F0.wireOp",EDGE,"E25.1");var subQ2=sQuery(id+"F0.wireOp",EDGE,"E25.6");var subQ3=sQuery(id+"F0.wireOp",EDGE,"E25.5");var subQ4=sQuery(id+"F0.wireOp",EDGE,"E25.4");var subQ5=sQuery(id+"F0.wireOp",EDGE,"E25.0");var subQ6=sQuery(id+"F0.wireOp",EDGE,"E25.2");var subQ7=sQuery(id+"F0.wireOp",EDGE,"E25.3");Q4=makeQuery(id+"F8.boolean.opBoolean","INTERSECT",EDGE,{"derivedFrom":[makeQuery(id+"F5.boolean.opBoolean","SPLIT",FACE,{"disambiguationData":[TD([makeQuery(id+"F2.opExtrude","SWEPT_FACE",FACE,{"disambiguationData":[OSD([subQ5])]})])],"derivedFrom":makeQuery(id+"F3.boolean.opBoolean","COPY",FACE,{"derivedFrom":makeQuery(id+"F3.opExtrude","CAP_FACE",FACE,{"disambiguationData":[OSD([subQ5,subQ1,subQ6,subQ7,subQ4,subQ3,subQ2,subQ0])],"isStart":false})})}),makeQuery(id+"F8.opExtrude","SWEPT_FACE",FACE,{"disambiguationData":[OSD([sQuery(id+"F7.wireOp",EDGE,"E67")])]})]});}
            var Q5;
            Q5=makeQuery(id+"F8.boolean.opBoolean","INTERSECT",EDGE,{"disambiguationData":[OD(0.0)],"derivedFrom":[makeQuery(id+"F5.opExtrude","SWEPT_FACE",FACE,{"disambiguationData":[OSD([sQuery(id+"F4.wireOp",EDGE,"E30")])]}),makeQuery(id+"F8.opExtrude","SWEPT_FACE",FACE,{"disambiguationData":[OSD([sQuery(id+"F7.wireOp",EDGE,"E67")])]})]});
            fillet(context, id + "F14", {"entities" : qUnion([Q0, Q1, Q2, Q3, Q4, Q5]), "radius" : 3 * mm, "tangentPropagation" : true, "allowEdgeOverflow" : false});
        }
        {
            var Q0;
            Q0=makeQuery(id+"F1.opExtrude","CAP_EDGE",EDGE,{"disambiguationData":[OSD([sQuery(id+"F0.wireOp",EDGE,"E1.bottom")])],"isStart":false});
            fillet(context, id + "F15", {"entities" : qUnion([Q0]), "radius" : 2 * mm, "tangentPropagation" : true, "allowEdgeOverflow" : false});
        }
        {
            var Q0;
            {var subQ0=sQuery(id+"F0.wireOp",EDGE,"E22.filletArc");var subQ1=sQuery(id+"F0.wireOp",EDGE,"E7");var subQ2=sQuery(id+"F0.wireOp",EDGE,"E6");var subQ3=sQuery(id+"F0.wireOp",EDGE,"E5");var subQ4=sQuery(id+"F0.wireOp",EDGE,"E4");var subQ5=sQuery(id+"F0.wireOp",EDGE,"E1.bottom");var subQ6=sQuery(id+"F0.wireOp",EDGE,"E21.filletArc");var subQ7=sQuery(id+"F0.wireOp",EDGE,"E1.top");var subQ8=sQuery(id+"F0.wireOp",EDGE,"E1.left");var subQ9=sQuery(id+"F0.wireOp",EDGE,"E1.right");var subQ10=sQuery(id+"F0.wireOp",EDGE,"E23.filletArc");var subQ11=sQuery(id+"F0.wireOp",EDGE,"E24.filletArc");Q0=makeQuery(id+"F2.boolean.opBoolean","SPLIT",FACE,{"disambiguationData":[TD([makeQuery(id+"F1.opExtrude","SWEPT_FACE",FACE,{"disambiguationData":[OSD([subQ5])]})])],"derivedFrom":makeQuery(id+"F1.opExtrude","CAP_FACE",FACE,{"disambiguationData":[OSD([subQ5,subQ7,subQ8,subQ9,subQ4,subQ3,subQ2,subQ1,subQ6,subQ0,subQ10,subQ11])],"isStart":true})});}
            var sketch = newSketch(context, id + "F16", { "sketchPlane" : qUnion([Q0])});
            skLineSegment(sketch, "E79.0", {"start": v(-70, 135) * mm, "end": v(70, 135) * mm});
            skArc(sketch, "E79.1", {"start": v(80, 125) * mm, "mid": v(77.07, 132.07) * mm, "end": v(70, 135) * mm});
            skLineSegment(sketch, "E79.2", {"start": v(80, -125) * mm, "end": v(80, 125) * mm});
            skLineSegment(sketch, "E79.3", {"start": v(-70, -135) * mm, "end": v(70, -135) * mm});
            skCircle(sketch, "E79.4", {"center": v(60, -101.25) * mm, "radius": 4 * mm});
            skArc(sketch, "E79.5", {"start": v(70, -135) * mm, "mid": v(77.07, -132.07) * mm, "end": v(80, -125) * mm});
            skLineSegment(sketch, "E79.6", {"start": v(-80, -125) * mm, "end": v(-80, 125) * mm});
            skCircle(sketch, "E79.7", {"center": v(-60, 101.25) * mm, "radius": 4 * mm});
            skArc(sketch, "E79.8", {"start": v(-70, 135) * mm, "mid": v(-77.07, 132.07) * mm, "end": v(-80, 125) * mm});
            skArc(sketch, "E79.9", {"start": v(-80, -125) * mm, "mid": v(-77.07, -132.07) * mm, "end": v(-70, -135) * mm});
            skCircle(sketch, "E79.10", {"center": v(-60, -101.25) * mm, "radius": 4 * mm});
            skLineSegment(sketch, "E80", {"start": v(0, 135) * mm, "end": v(0, 165) * mm, "construction": true});
            skCircle(sketch, "E81", {"center": v(0, 165) * mm, "radius": 6 * mm});
            skArc(sketch, "E82", {"start": v(-15, 165) * mm, "mid": v(0, 180) * mm, "end": v(15, 165) * mm});
            skLineSegment(sketch, "E83", {"start": v(15, 165) * mm, "end": v(15, 153) * mm});
            skLineSegment(sketch, "E84", {"start": v(-15, 165) * mm, "end": v(-15, 153) * mm});
            skLineSegment(sketch, "E85.0.0", {"start": v(70, 135) * mm, "end": v(-70, 135) * mm});
            skLineSegment(sketch, "E85.0.2", {"start": v(-80, 125) * mm, "end": v(-80, -125) * mm});
            skLineSegment(sketch, "E86", {"start": v(15, 153) * mm, "end": v(33, 135) * mm});
            skLineSegment(sketch, "E87", {"start": v(-15, 153) * mm, "end": v(-33, 135) * mm});
            skArc(sketch, "E88.MirrorCS", {"start": v(-15, -435) * mm, "mid": v(0, -435.62) * mm, "end": v(15, -435) * mm});
            skCircle(sketch, "E89.MirrorC", {"center": v(0, -435) * mm, "radius": 6 * mm});
            skLineSegment(sketch, "E90.MirrorCS", {"start": v(-15, -435) * mm, "end": v(-15, -423) * mm});
            skLineSegment(sketch, "E91.MirrorCS", {"start": v(15, -435) * mm, "end": v(15, -423) * mm});
            skLineSegment(sketch, "E92.MirrorCS", {"start": v(15, -423) * mm, "end": v(33, -405) * mm});
            skLineSegment(sketch, "E93.MirrorCS", {"start": v(-15, -423) * mm, "end": v(-33, -405) * mm});
            skLineSegment(sketch, "E94", {"start": v(-80, 0) * mm, "end": v(80, 0) * mm, "construction": true});
            skArc(sketch, "E95.MirrorCS", {"start": v(-15, -165) * mm, "mid": v(0, -180) * mm, "end": v(15, -165) * mm});
            skLineSegment(sketch, "E96.MirrorCS", {"start": v(-15, -165) * mm, "end": v(-15, -153) * mm});
            skLineSegment(sketch, "E97.MirrorCS", {"start": v(15, -165) * mm, "end": v(15, -153) * mm});
            skCircle(sketch, "E98.MirrorC", {"center": v(0, -165) * mm, "radius": 6 * mm});
            skLineSegment(sketch, "E99.MirrorCS", {"start": v(15, -153) * mm, "end": v(33, -135) * mm});
            skLineSegment(sketch, "E100.MirrorCS", {"start": v(-15, -153) * mm, "end": v(-33, -135) * mm});
            skSolve(sketch);
        }
        {
            var Q0;
            Q0=makeQuery(id+"F16.imprint","IMPRINT",FACE,{"disambiguationData":[TD([[makeQuery(id+"F16.imprint","IMPRINT",EDGE,{"derivedFrom":sQuery(id+"F16.wireOp",EDGE,"E79.4")}),-1.0]])]});
            var Q1;
            Q1=makeQuery(id+"F16.imprint","IMPRINT",FACE,{"disambiguationData":[TD([[makeQuery(id+"F16.imprint","IMPRINT",EDGE,{"derivedFrom":sQuery(id+"F16.wireOp",EDGE,"E81")}),-1.0]])]});
            var Q2;
            Q2=makeQuery(id+"F16.imprint","IMPRINT",FACE,{"disambiguationData":[TD([[makeQuery(id+"F16.imprint","IMPRINT",EDGE,{"derivedFrom":sQuery(id+"F16.wireOp",EDGE,"E95.MirrorCS")}),1.0]])]});
            extrude(context, id + "F17", {"entities" : qUnion([Q0, Q1, Q2]), "depth" : 5 * mm});
        }
    });
